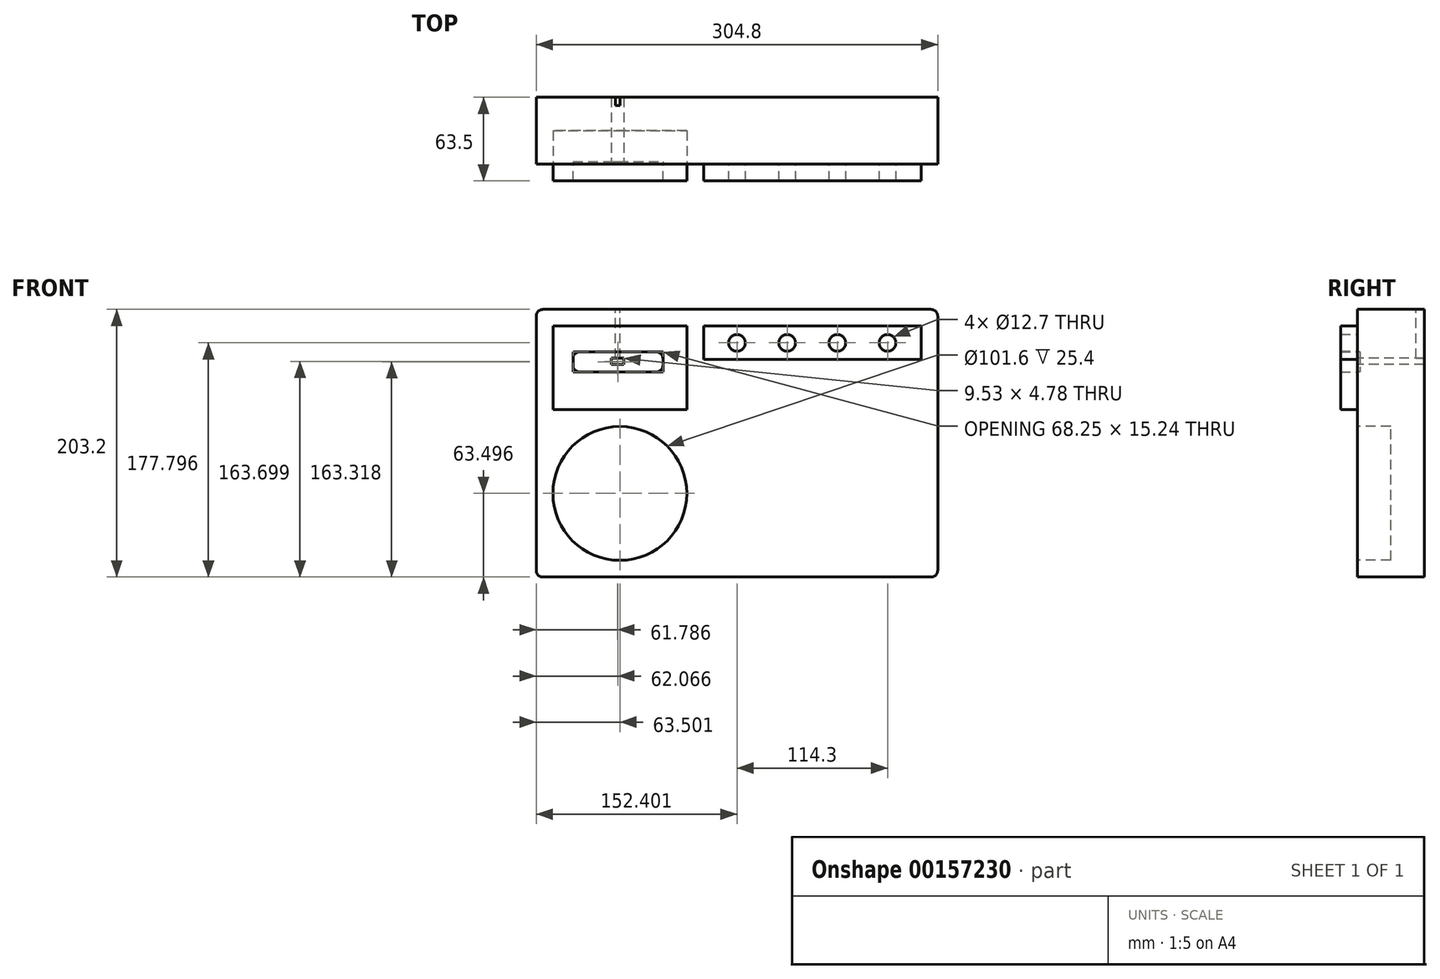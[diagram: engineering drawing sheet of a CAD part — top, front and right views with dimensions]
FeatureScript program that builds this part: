
annotation { "Feature Type Name" : "Feature", "Feature Type Description" : "" }
export const myFeature = defineFeature(function(context is Context, id is Id, definition is map)
    precondition{}
    {
        {
            var Q0;
            Q0=qCreatedBy(makeId("Front.planeOp"),FACE);
            var sketch = newSketch(context, id + "F0", { "sketchPlane" : qUnion([Q0])});
            skLineSegment(sketch, "E0.bottom", {"start": v(156.21, -101.12) * mm, "end": v(-148.59, -101.12) * mm});
            skLineSegment(sketch, "E0.top", {"start": v(156.21, 102.08) * mm, "end": v(-148.59, 102.08) * mm});
            skLineSegment(sketch, "E0.left", {"start": v(156.21, -101.12) * mm, "end": v(156.21, 102.08) * mm});
            skLineSegment(sketch, "E0.right", {"start": v(-148.59, -101.12) * mm, "end": v(-148.59, 102.08) * mm});
            skLineSegment(sketch, "E1.bottom", {"start": v(-91.57, 64.97) * mm, "end": v(-82.04, 64.97) * mm});
            skLineSegment(sketch, "E1.top", {"start": v(-91.57, 60.2) * mm, "end": v(-82.04, 60.2) * mm});
            skLineSegment(sketch, "E1.left", {"start": v(-91.57, 64.97) * mm, "end": v(-91.57, 60.2) * mm});
            skLineSegment(sketch, "E1.right", {"start": v(-82.04, 64.97) * mm, "end": v(-82.04, 60.2) * mm});
            skLineSegment(sketch, "E2.bottom", {"start": v(-88.34, 64.97) * mm, "end": v(-85.3, 64.97) * mm});
            skLineSegment(sketch, "E2.top", {"start": v(-88.34, 102.08) * mm, "end": v(-85.3, 102.08) * mm});
            skSolve(sketch);
        }
        {
            var Q0;
            Q0=makeQuery(id+"F0.imprint","IMPRINT",FACE,{"disambiguationData":[TD([[makeQuery(id+"F0.imprint","IMPRINT",EDGE,{"derivedFrom":sQuery(id+"F0.wireOp",EDGE,"E0.bottom")}),-1.0]])]});
            var sketch = newSketch(context, id + "F1", { "sketchPlane" : qUnion([Q0])});
            skCircle(sketch, "E3", {"center": v(-85.09, -37.62) * mm, "radius": 50.8 * mm});
            skSolve(sketch);
        }
        {
            var Q0;
            Q0=makeQuery(id+"F0.imprint","IMPRINT",FACE,{"disambiguationData":[TD([[makeQuery(id+"F0.imprint","IMPRINT",EDGE,{"derivedFrom":sQuery(id+"F0.wireOp",EDGE,"E0.bottom")}),-1.0]])]});
            var sketch = newSketch(context, id + "F2", { "sketchPlane" : qUnion([Q0])});
            skLineSegment(sketch, "E4.bottom", {"start": v(118.11, 13.18) * mm, "end": v(143.51, 13.18) * mm});
            skLineSegment(sketch, "E4.top", {"start": v(118.11, -88.42) * mm, "end": v(143.51, -88.42) * mm});
            skLineSegment(sketch, "E4.right", {"start": v(143.51, 13.18) * mm, "end": v(143.51, -88.42) * mm});
            skArc(sketch, "E5", {"start": v(118.21, 0) * mm, "mid": v(126.42, 6.13) * mm, "end": v(118.11, 12.11) * mm});
            skLineSegment(sketch, "E6", {"start": v(118.11, 13.18) * mm, "end": v(118.11, 12.11) * mm});
            skLineSegment(sketch, "E7", {"start": v(118.21, 0) * mm, "end": v(118.11, -88.42) * mm});
            skSolve(sketch);
        }
        {
            var Q0;
            Q0=makeQuery(id+"F2.imprint","IMPRINT",FACE,{"disambiguationData":[TD([[makeQuery(id+"F2.imprint","IMPRINT",EDGE,{"derivedFrom":sQuery(id+"F2.wireOp",EDGE,"E4.bottom")}),1.0]])]});
            var sketch = newSketch(context, id + "F3", { "sketchPlane" : qUnion([Q0])});
            skLineSegment(sketch, "E8.bottom", {"start": v(-21.59, 89.38) * mm, "end": v(143.51, 89.38) * mm});
            skLineSegment(sketch, "E8.top", {"start": v(-21.59, 63.98) * mm, "end": v(143.51, 63.98) * mm});
            skLineSegment(sketch, "E8.left", {"start": v(-21.59, 89.38) * mm, "end": v(-21.59, 63.98) * mm});
            skLineSegment(sketch, "E8.right", {"start": v(143.51, 89.38) * mm, "end": v(143.51, 63.98) * mm});
            skCircle(sketch, "E9", {"center": v(3.81, 76.68) * mm, "radius": 6.35 * mm});
            skCircle(sketch, "E10", {"center": v(41.91, 76.68) * mm, "radius": 6.35 * mm});
            skCircle(sketch, "E11", {"center": v(80.01, 76.68) * mm, "radius": 6.35 * mm});
            skCircle(sketch, "E12", {"center": v(118.11, 76.68) * mm, "radius": 6.35 * mm});
            skSolve(sketch);
        }
        {
            var Q0;
            Q0=makeQuery(id+"F0.imprint","IMPRINT",FACE,{"disambiguationData":[TD([[makeQuery(id+"F0.imprint","IMPRINT",EDGE,{"derivedFrom":sQuery(id+"F0.wireOp",EDGE,"E0.bottom")}),-1.0]])]});
            var sketch = newSketch(context, id + "F4", { "sketchPlane" : qUnion([Q0])});
            skLineSegment(sketch, "E13.bottom", {"start": v(-135.89, 89.38) * mm, "end": v(-34.29, 89.38) * mm});
            skLineSegment(sketch, "E13.top", {"start": v(-135.89, 25.88) * mm, "end": v(-34.29, 25.88) * mm});
            skLineSegment(sketch, "E13.left", {"start": v(-135.89, 89.38) * mm, "end": v(-135.89, 25.88) * mm});
            skLineSegment(sketch, "E13.right", {"start": v(-34.29, 89.38) * mm, "end": v(-34.29, 25.88) * mm});
            skLineSegment(sketch, "E14.bottom", {"start": v(-120.65, 69.82) * mm, "end": v(-52.4, 69.82) * mm});
            skLineSegment(sketch, "E14.top", {"start": v(-120.65, 54.58) * mm, "end": v(-52.4, 54.58) * mm});
            skLineSegment(sketch, "E14.left", {"start": v(-120.65, 69.82) * mm, "end": v(-120.65, 54.58) * mm});
            skLineSegment(sketch, "E14.right", {"start": v(-52.4, 69.82) * mm, "end": v(-52.4, 54.58) * mm});
            skSolve(sketch);
        }
        {
            var Q0;
            Q0=makeQuery(id+"F4.imprint","IMPRINT",FACE,{"disambiguationData":[TD([[makeQuery(id+"F4.imprint","IMPRINT",EDGE,{"derivedFrom":sQuery(id+"F4.wireOp",EDGE,"E13.bottom")}),-1.0]])]});
            extrude(context, id + "F5", {"entities" : qUnion([Q0]), "depth" : 12.7 * mm});
        }
        {
            var Q0;
            Q0=makeQuery(id+"F4.imprint","IMPRINT",FACE,{"disambiguationData":[TD([[makeQuery(id+"F4.imprint","IMPRINT",EDGE,{"derivedFrom":sQuery(id+"F4.wireOp",EDGE,"E14.bottom")}),-1.0]])]});
            extrude(context, id + "F6", {"entities" : qUnion([Q0]), "oppositeDirection" : true, "depth" : 1.9 * mm});
        }
        {
            var Q0;
            Q0 = qSketchRegion(id + "F3", true);
            extrude(context, id + "F7", {"entities" : qUnion([Q0]), "depth" : 12.7 * mm});
        }
        {
            var Q0;
            Q0 = qSketchRegion(id + "F0", true);
            extrude(context, id + "F8", {"entities" : qUnion([Q0]), "oppositeDirection" : true, "depth" : 50.8 * mm});
        }
        {
            var Q0;
            Q0=makeQuery(id+"F1.imprint","IMPRINT",FACE,{"disambiguationData":[TD([[makeQuery(id+"F1.imprint","IMPRINT",EDGE,{"derivedFrom":sQuery(id+"F1.wireOp",EDGE,"E3")}),1.0]])]});
            var Q1;
            Q1=sQuery(id+"F1.wireOp",EDGE,"E3");
            extrude(context, id + "F9", {"entities" : qUnion([Q0]), "operationType" : NewBodyOperationType.REMOVE, "surfaceEntities" : qUnion([Q1]), "oppositeDirection" : true, "depth" : 25.4 * mm});
        }
        {
            var Q0;
            Q0=makeQuery(id+"F8.opExtrude","SWEPT_EDGE",EDGE,{"disambiguationData":[OSD([sQuery(id+"F0.wireOp",EDGE,"E0.bottom"),sQuery(id+"F0.wireOp",EDGE,"E0.left")])]});
            fillet(context, id + "F10", {"entities" : qUnion([Q0]), "radius" : 5.08 * mm, "tangentPropagation" : true, "allowEdgeOverflow" : false});
        }
        {
            var Q0;
            Q0=makeQuery(id+"F8.opExtrude","SWEPT_EDGE",EDGE,{"disambiguationData":[OSD([sQuery(id+"F0.wireOp",EDGE,"E0.top"),sQuery(id+"F0.wireOp",EDGE,"E0.left")])]});
            fillet(context, id + "F11", {"entities" : qUnion([Q0]), "radius" : 5.08 * mm, "tangentPropagation" : true, "allowEdgeOverflow" : false});
        }
        {
            var Q0;
            Q0=makeQuery(id+"F8.opExtrude","SWEPT_EDGE",EDGE,{"disambiguationData":[OSD([sQuery(id+"F0.wireOp",EDGE,"E0.bottom"),sQuery(id+"F0.wireOp",EDGE,"E0.right")])]});
            fillet(context, id + "F12", {"entities" : qUnion([Q0]), "radius" : 5.08 * mm, "tangentPropagation" : true, "allowEdgeOverflow" : false});
        }
        {
            var Q0;
            Q0=makeQuery(id+"F8.opExtrude","SWEPT_EDGE",EDGE,{"disambiguationData":[OSD([sQuery(id+"F0.wireOp",EDGE,"E0.top"),sQuery(id+"F0.wireOp",EDGE,"E0.right")])]});
            fillet(context, id + "F13", {"entities" : qUnion([Q0]), "radius" : 5.08 * mm, "tangentPropagation" : true, "allowEdgeOverflow" : false});
        }
        {
            var Q0;
            Q0=makeQuery(id+"F8.opExtrude","CAP_FACE",FACE,{"disambiguationData":[OSD([sQuery(id+"F0.wireOp",EDGE,"E0.bottom"),sQuery(id+"F0.wireOp",EDGE,"E0.top"),sQuery(id+"F0.wireOp",EDGE,"E0.left"),sQuery(id+"F0.wireOp",EDGE,"E0.right"),sQuery(id+"F0.wireOp",EDGE,"E1.bottom"),sQuery(id+"F0.wireOp",EDGE,"E1.top"),sQuery(id+"F0.wireOp",EDGE,"E1.left"),sQuery(id+"F0.wireOp",EDGE,"E1.right"),sQuery(id+"F0.wireOp",EDGE,"E2.bottom"),sQuery(id+"F0.wireOp",EDGE,"E2.top")])],"isStart":false});
            var sketch = newSketch(context, id + "F14", { "sketchPlane" : qUnion([Q0])});
            skLineSegment(sketch, "E15", {"start": v(84.92, 64.97) * mm, "end": v(84.92, 102.08) * mm});
            skLineSegment(sketch, "E16", {"start": v(88.42, 64.97) * mm, "end": v(88.42, 102.08) * mm});
            skSolve(sketch);
        }
        {
            var Q0;
            {var subQ0=sQuery(id+"F14.wireOp",EDGE,"E15");Q0=makeQuery(id+"F14.imprint","IMPRINT",FACE,{"disambiguationData":[TD([[makeQuery(id+"F14.imprint","IMPRINT",EDGE,{"derivedFrom":subQ0}),-1.0]])]});}
            extrude(context, id + "F15", {"entities" : qUnion([Q0]), "operationType" : NewBodyOperationType.REMOVE, "oppositeDirection" : true, "depth" : 6.35 * mm});
        }
        {
            var Q0;
            Q0=makeQuery(id+"F5.opExtrude","SWEPT_EDGE",EDGE,{"disambiguationData":[OSD([sQuery(id+"F4.wireOp",EDGE,"E14.bottom"),sQuery(id+"F4.wireOp",EDGE,"E14.left")])]});
            var Q1;
            Q1=makeQuery(id+"F5.opExtrude","SWEPT_EDGE",EDGE,{"disambiguationData":[OSD([sQuery(id+"F4.wireOp",EDGE,"E14.bottom"),sQuery(id+"F4.wireOp",EDGE,"E14.right")])]});
            var Q2;
            Q2=makeQuery(id+"F5.opExtrude","SWEPT_EDGE",EDGE,{"disambiguationData":[OSD([sQuery(id+"F4.wireOp",EDGE,"E14.top"),sQuery(id+"F4.wireOp",EDGE,"E14.left")])]});
            var Q3;
            Q3=makeQuery(id+"F5.opExtrude","SWEPT_EDGE",EDGE,{"disambiguationData":[OSD([sQuery(id+"F4.wireOp",EDGE,"E14.top"),sQuery(id+"F4.wireOp",EDGE,"E14.right")])]});
            fillet(context, id + "F16", {"entities" : qUnion([Q0, Q1, Q2, Q3]), "radius" : 5.08 * mm, "tangentPropagation" : true, "allowEdgeOverflow" : false});
        }
    });
